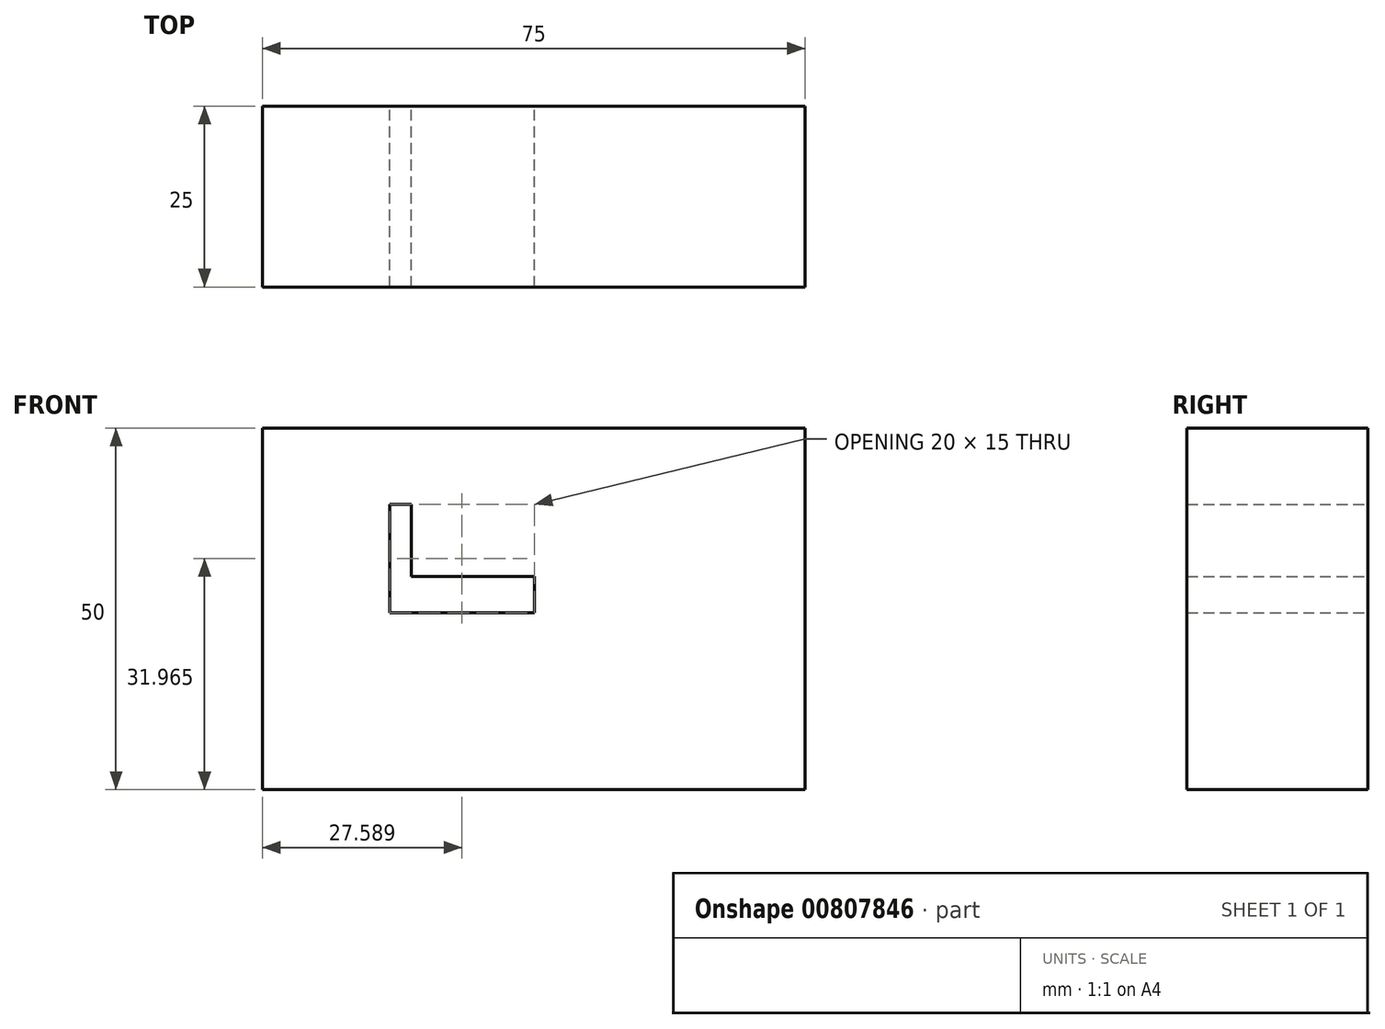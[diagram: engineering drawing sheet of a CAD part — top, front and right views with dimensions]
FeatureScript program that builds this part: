
annotation { "Feature Type Name" : "Feature", "Feature Type Description" : "" }
export const myFeature = defineFeature(function(context is Context, id is Id, definition is map)
    precondition{}
    {
        {
            var Q0;
            Q0=qCreatedBy(makeId("Front.planeOp"),FACE);
            var sketch = newSketch(context, id + "F0", { "sketchPlane" : qUnion([Q0])});
            skLineSegment(sketch, "E0.bottom", {"start": v(-40.37, 32.68) * mm, "end": v(34.63, 32.68) * mm});
            skLineSegment(sketch, "E0.top", {"start": v(-40.37, -17.32) * mm, "end": v(34.63, -17.32) * mm});
            skLineSegment(sketch, "E0.left", {"start": v(-40.37, 32.68) * mm, "end": v(-40.37, -17.32) * mm});
            skLineSegment(sketch, "E0.right", {"start": v(34.63, 32.68) * mm, "end": v(34.63, -17.32) * mm});
            skSolve(sketch);
        }
        {
            var Q0;
            Q0=makeQuery(id+"F0.imprint","IMPRINT",FACE,{"disambiguationData":[TD([[makeQuery(id+"F0.imprint","IMPRINT",EDGE,{"derivedFrom":sQuery(id+"F0.wireOp",EDGE,"E0.bottom")}),-1.0]])]});
            extrude(context, id + "F1", {"entities" : qUnion([Q0]), "depth" : 25 * mm, "offsetDistance" : 25 * mm});
        }
        {
            var Q0;
            Q0=qCreatedBy(makeId("Front.planeOp"),FACE);
            var sketch = newSketch(context, id + "F2", { "sketchPlane" : qUnion([Q0])});
            skLineSegment(sketch, "E1", {"start": v(-22.78, 22.14) * mm, "end": v(-22.78, 7.14) * mm});
            skLineSegment(sketch, "E2", {"start": v(-22.78, 7.14) * mm, "end": v(-2.78, 7.14) * mm});
            skLineSegment(sketch, "E3", {"start": v(-2.78, 7.14) * mm, "end": v(-2.78, 12.14) * mm});
            skLineSegment(sketch, "E4", {"start": v(-2.78, 12.14) * mm, "end": v(-19.78, 12.14) * mm});
            skLineSegment(sketch, "E5", {"start": v(-19.78, 12.14) * mm, "end": v(-19.78, 22.14) * mm});
            skLineSegment(sketch, "E6", {"start": v(-19.78, 22.14) * mm, "end": v(-22.78, 22.14) * mm});
            skSolve(sketch);
        }
        {
            var Q0;
            Q0 = qSketchRegion(id + "F2", true);
            extrude(context, id + "F3", {"entities" : qUnion([Q0]), "operationType" : NewBodyOperationType.REMOVE, "depth" : 25 * mm, "offsetDistance" : 25 * mm});
        }
    });
